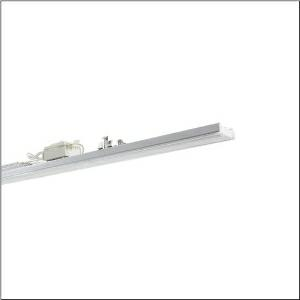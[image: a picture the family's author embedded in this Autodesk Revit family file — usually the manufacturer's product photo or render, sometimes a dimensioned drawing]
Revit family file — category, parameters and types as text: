
# Revit family: licross_21_recessed_ho_52tl1wdv4l2m
name_source: partatom
category: Lighting Fixtures
units: mm (PartAtom-declared; Revit-internal decimal feet)

## family parameters
Cut with Voids When Loaded = No
Host = Face
Light Source = No
Part Type = Normal
Room Calculation Point = No
Round Connector Dimension = Use Diameter
Shared = No

## types (1)
- --- (1 x LED, 22780 lm, 125.6 W, 4000K)
    Apparent Load = 126 VA
    CIE Flux Codes = 73 94 99 100 100
    Color Rendering = 80
    Color Temperature = 4000K
    Default Elevation = 1800 mm
    Description = Licross 21 Recessed HO, luminaire insert, of sheet steel, galvanised, coil coated, white, length: 2.250mm, width: 66mm, height: 67mm, LED rated luminous flux: 22.780lm, light colour: 840, SDCM (Standard Deviation of Colour Matching)MacAdam ≤ 3 SDCM (initial), control gear: DALI 2, with plug, 5-pole, with phase selection, mains connection: 220..240V, AC, 50/60Hz, rated input power: 126W, internal wiring halogen-free, primary optical cover: cover, of PMMA, light emission: direct distribution, primary light characteristic: symmetric, protection rating (complete): IP40, insulation class (complete): insulation class I (protective earthing), certification: CE, ENEC, VDE, UKCA, protection symbol: D if used in an environment without relevant dust loads with corresponding accessories, impact resistance: IK06, permissible ambient temperature for indoor applications: -40..+30°C, corresponds to IFS (International Featured Standards) requirements for safety and quality in the food industry, reducing of maximum allowable ambient temperature of 5°C with ceiling mounting, LABS conformity tested according to VDMA 24364:2018-05, The light source and the operating device comply with the requirements of the Ecodesign Regulation (EU) 2019/2020 and are replaceable in accordance with this regulation, packaging unit: 1 piece
    Height = 58 mm
    Lamp = 1 x LED
    Lamp Light Flux = 22780 lm
    Lamp Power = 125.6 W
    Lamp count = 1
    Length = 2250 mm
    Luminous efficacy = 181 lm/W
    Manufacturer = Siteco
    ModVariant = No
    Model = 52TL1WDV4L2M
    Mounting Place = Ceiling
    Mounting Type = Pendant
    Number of Poles = 1
    OnlyDefault = Yes
    Power Factor = 1
    Product Name = Licross 21 Recessed HO
    Product group = luminaire insert | ceiling pendant
    ProductGroupID = 901
    Protection Class = Protection class I
    Protection Degree = IP 40
    RLX_Detail_Level = 1
    RLX_Emergency_Light_Flux = 0 lm
    RLX_Emergency_Type = 0
    RLX_Emergency_Type_DB = No
    RlxData = <blob elided: 29789 chars, md5=00496e92>
    Socket = socket
    Standby Power = 0 W
    System Light Flux = 22780 lm
    System Power = 126 W
    Type Comments = factory setting: luminous flux: 100 % | dim-lin: 254 | 489 mA
    Type Image = l_1296930.jpg
    URL = http://relux.com
    VarID = @adj_066553
    Voltage = 0 V
    Weight = 0.00 kg
    Width = 66 mm

## geometry (parser evidence)
native form markers: Blend x4, Sweep x8
no freeform markers — native parametric forms only
